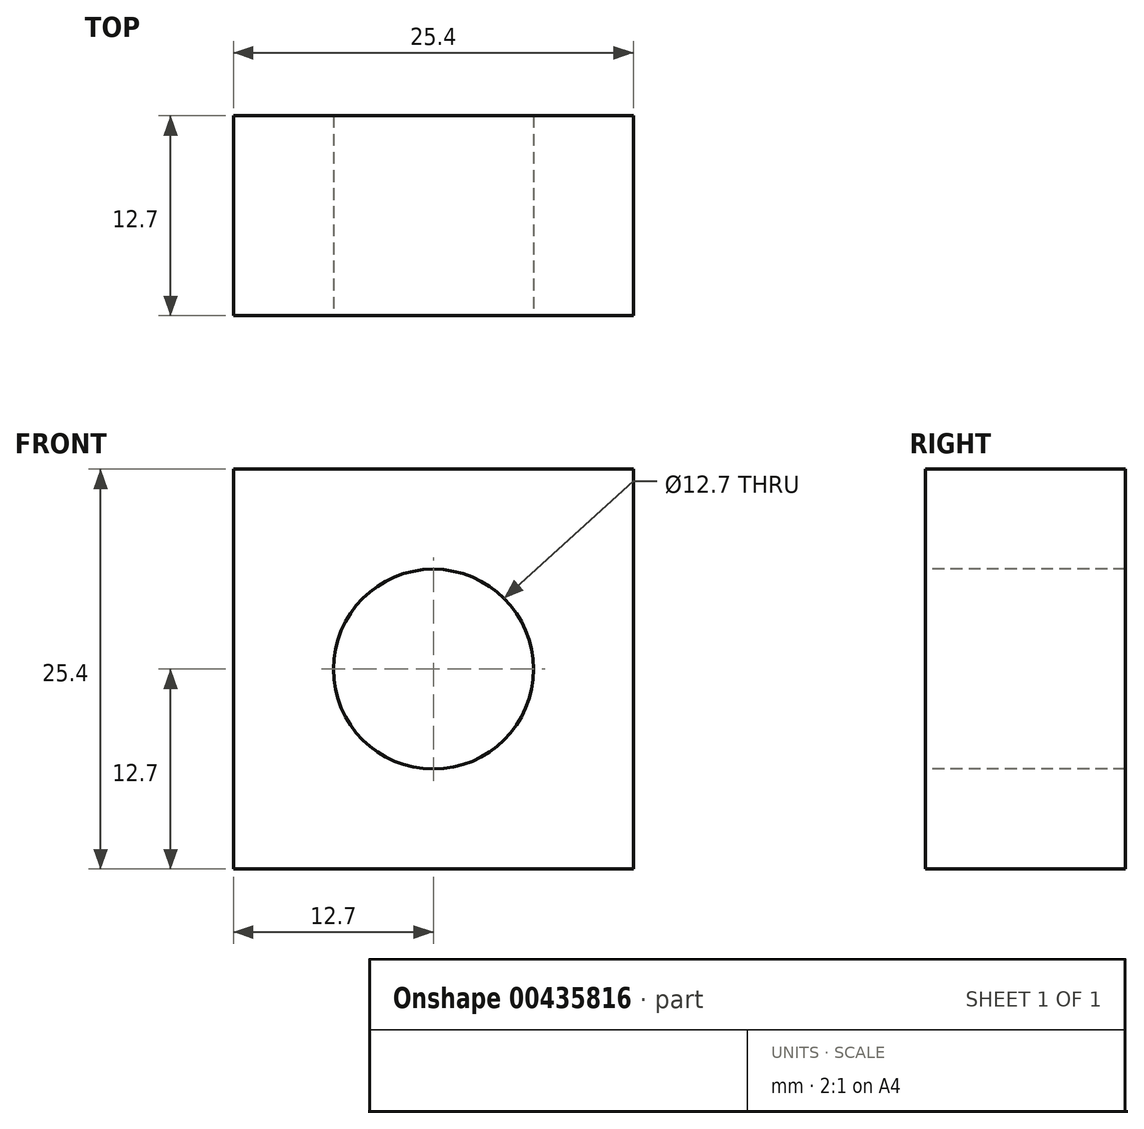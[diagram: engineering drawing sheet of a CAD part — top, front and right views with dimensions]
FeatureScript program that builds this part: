
annotation { "Feature Type Name" : "Feature", "Feature Type Description" : "" }
export const myFeature = defineFeature(function(context is Context, id is Id, definition is map)
    precondition{}
    {
        {
            var Q0;
            Q0=qCreatedBy(makeId("Front.planeOp"),FACE);
            var sketch = newSketch(context, id + "F0", { "sketchPlane" : qUnion([Q0])});
            skLineSegment(sketch, "E0.bottom", {"start": v(12.7, 12.7) * mm, "end": v(-12.7, 12.7) * mm});
            skLineSegment(sketch, "E0.top", {"start": v(12.7, -12.7) * mm, "end": v(-12.7, -12.7) * mm});
            skLineSegment(sketch, "E0.left", {"start": v(12.7, 12.7) * mm, "end": v(12.7, -12.7) * mm});
            skLineSegment(sketch, "E0.right", {"start": v(-12.7, 12.7) * mm, "end": v(-12.7, -12.7) * mm});
            skPoint(sketch, "E0.middle", {"position": v(0, 0) * mm});
            skCircle(sketch, "E1", {"center": v(0, 0) * mm, "radius": 6.35 * mm});
            skSolve(sketch);
        }
        {
            var Q0;
            Q0=makeQuery(id+"F0.imprint","IMPRINT",FACE,{"disambiguationData":[TD([[makeQuery(id+"F0.imprint","IMPRINT",EDGE,{"derivedFrom":sQuery(id+"F0.wireOp",EDGE,"E0.bottom")}),1.0]])]});
            extrude(context, id + "F1", {"entities" : qUnion([Q0]), "endBound" : BoundingType.SYMMETRIC, "oppositeDirection" : true, "depth" : 12.7 * mm});
        }
    });
